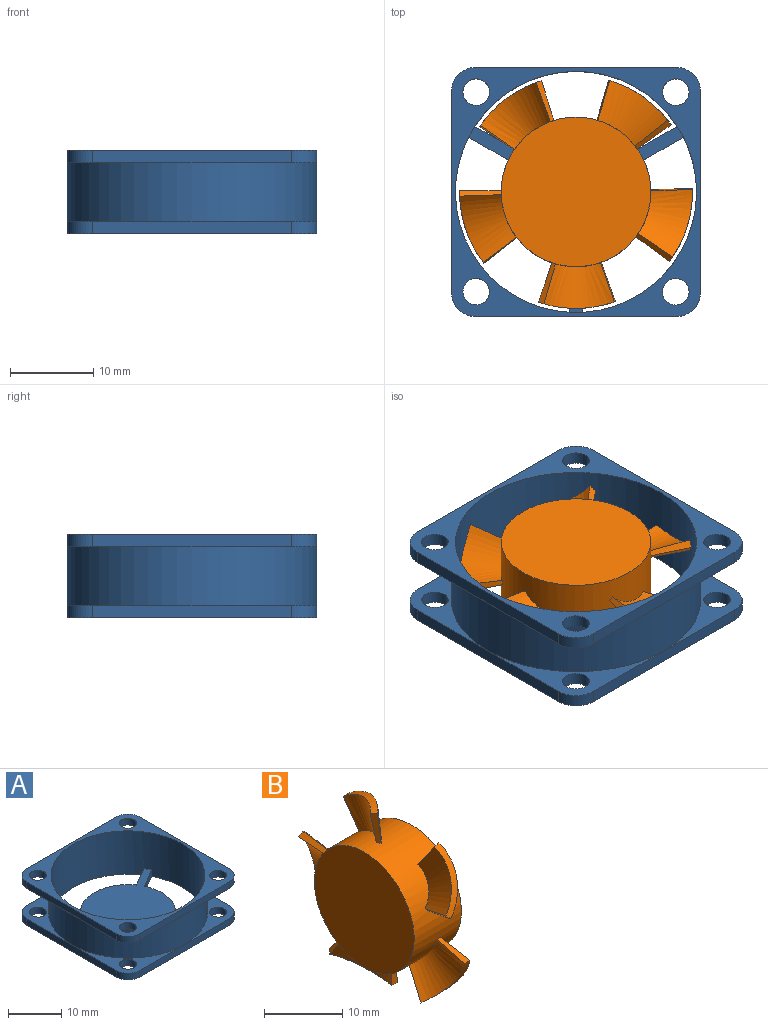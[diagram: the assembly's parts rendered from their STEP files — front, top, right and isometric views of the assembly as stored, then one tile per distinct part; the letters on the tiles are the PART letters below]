
ASSEMBLY  parts=2 mates=1
PART A: 46 faces, bbox 30x30x10 mm
  f0: cylinder r=9mm len=12.8mm, axis (0,0,-1), area 26mm2, adj f11,f37,f39,f41
  f1: cylinder r=1.6mm len=3.2mm, axis (0,0,-1), area 15.1mm2, adj f11,f13
  f2: cylinder r=1.6mm len=3.2mm, axis (0,0,-1), area 15.1mm2, adj f12,f14
  f3: cylinder r=1.6mm len=3.2mm, axis (0,0,-1), area 15.1mm2, adj f11,f15
  f4: cylinder r=1.6mm len=3.2mm, axis (0,0,-1), area 15.1mm2, adj f12,f16
  f5: cylinder r=1.6mm len=3.2mm, axis (0,0,-1), area 15.1mm2, adj f11,f17
  f6: cylinder r=1.6mm len=3.2mm, axis (0,0,-1), area 15.1mm2, adj f12,f18
  f7: cylinder r=1.6mm len=3.2mm, axis (0,0,-1), area 15.1mm2, adj f11,f19
  f8: cylinder r=1.6mm len=3.2mm, axis (0,0,-1), area 15.1mm2, adj f12,f20
  f9: cylinder r=15mm len=30mm, axis (0,0,1), area 659.7mm2, adj f13,f14,f15,f16,f17,f18,f19,f20
  f10: cylinder r=14.5mm len=29mm, axis (0,0,-1), area 904.3mm2, adj f11,f12,f37,f38,f39,f40,f41,f42
  f11: plane 30x30mm, normal (0,0,-1), area 478.8mm2, adj f0,f1,f3,f5,f7,f10,f21,f23
  f12: plane 30x30mm, normal (0,0,1), area 199.6mm2, adj f2,f4,f6,f8,f10,f22,f24,f26
  f13: plane 15x15mm, normal (0,0,1), area 38.3mm2, adj f1,f9,f25,f27,f29
  f14: plane 15x15mm, normal (0,0,-1), area 38.3mm2, adj f2,f9,f26,f28,f30
  f15: plane 15x15mm, normal (0,0,1), area 38.3mm2, adj f3,f9,f21,f23,f25
  f16: plane 15x15mm, normal (0,0,-1), area 38.3mm2, adj f4,f9,f22,f24,f26
  f17: plane 15x15mm, normal (0,0,1), area 38.3mm2, adj f5,f9,f21,f33,f35
  f18: plane 15x15mm, normal (0,0,-1), area 38.3mm2, adj f6,f9,f22,f34,f36
  f19: plane 15x15mm, normal (0,0,1), area 38.3mm2, adj f7,f9,f29,f31,f33
  f20: plane 15x15mm, normal (0,0,-1), area 38.3mm2, adj f8,f9,f30,f32,f34
  f21: plane 24x1.5mm, normal (0,-1,0), area 36mm2, adj f11,f15,f17,f23,f35
  f22: plane 24x1.5mm, normal (0,-1,0), area 36mm2, adj f12,f16,f18,f24,f36
  f23: cylinder r=3mm len=3mm, axis (0,0,-1), area 7.1mm2, adj f11,f15,f21,f25
  f24: cylinder r=3mm len=3mm, axis (0,0,-1), area 7.1mm2, adj f12,f16,f22,f26
  f25: plane 24x1.5mm, normal (-1,0,0), area 36mm2, adj f11,f13,f15,f23,f27
  f26: plane 24x1.5mm, normal (-1,0,0), area 36mm2, adj f12,f14,f16,f24,f28
  f27: cylinder r=3mm len=3mm, axis (0,0,-1), area 7.1mm2, adj f11,f13,f25,f29
  f28: cylinder r=3mm len=3mm, axis (0,0,-1), area 7.1mm2, adj f12,f14,f26,f30
  f29: plane 24x1.5mm, normal (0,1,0), area 36mm2, adj f11,f13,f19,f27,f31
  f30: plane 24x1.5mm, normal (0,1,0), area 36mm2, adj f12,f14,f20,f28,f32
  f31: cylinder r=3mm len=3mm, axis (0,0,-1), area 7.1mm2, adj f11,f19,f29,f33
  f32: cylinder r=3mm len=3mm, axis (0,0,-1), area 7.1mm2, adj f12,f20,f30,f34
  f33: plane 24x1.5mm, normal (1,0,0), area 36mm2, adj f11,f17,f19,f31,f35
  f34: plane 24x1.5mm, normal (1,0,0), area 36mm2, adj f12,f18,f20,f32,f36
  f35: cylinder r=3mm len=3mm, axis (0,0,-1), area 7.1mm2, adj f11,f17,f21,f33
  f36: cylinder r=3mm len=3mm, axis (0,0,-1), area 7.1mm2, adj f12,f18,f22,f34
  f37: plane 5.51x1.5mm, normal (-1,0,0), area 8.3mm2, adj f0,f10,f11,f39
  f38: plane 5.51x1.5mm, normal (1,0,0), area 8.3mm2, adj f10,f11,f39,f44
  f39: plane 25.83x23.5mm, normal (0,0,1), area 279.2mm2, adj f0,f10,f37,f38,f40,f41,f42,f43
  f40: plane 4.77x2.76mm, normal (0.5,0.87,0), area 8.3mm2, adj f10,f11,f39,f45
  f41: plane 4.77x2.76mm, normal (-0.5,-0.87,0), area 8.3mm2, adj f0,f10,f11,f39
  f42: plane 4.77x2.76mm, normal (0.5,-0.87,0), area 8.3mm2, adj f10,f11,f39,f44
  f43: plane 4.77x2.76mm, normal (-0.5,0.87,0), area 8.3mm2, adj f10,f11,f39,f45
  f44: cylinder r=9mm len=12.8mm, axis (0,0,-1), area 26mm2, adj f11,f38,f39,f42
  f45: cylinder r=9mm len=14.78mm, axis (0,0,-1), area 26mm2, adj f11,f39,f40,f43
PART B: 28 faces, bbox 8.5x28.2x28.9 mm
  f0: cylinder r=14mm len=8.81mm, axis (1,0,0), area 9.8mm2, adj f18,f19,f20,f21
  f1: cylinder r=9mm len=18mm, axis (-1,0,0), area 460.6mm2, adj f2,f3,f4,f5,f6,f7,f8,f9
  f2: bspline ~8.51x4.96mm, area 35.5mm2, adj f1,f3,f4,f27
  f3: plane 4.76x1.78mm, normal (-0.16,-0.32,-0.93), area 3.9mm2, adj f1,f2,f5,f27
  f4: plane 4.94x2.04mm, normal (-0.73,-0.32,0.61), area 3.9mm2, adj f1,f2,f5,f27
  f5: bspline ~9.27x4.79mm, area 38.4mm2, adj f1,f3,f4,f27
  f6: bspline ~8.28x6.82mm, area 36.8mm2, adj f1,f7,f8,f26
  f7: plane 4.05x3.14mm, normal (-0.16,0.79,-0.59), area 3.9mm2, adj f1,f6,f9,f26
  f8: plane 5.01x1.38mm, normal (-0.73,-0.68,-0.11), area 3.9mm2, adj f1,f6,f9,f26
  f9: bspline ~8.82x6.88mm, area 40.1mm2, adj f1,f7,f8,f26
  f10: bspline ~8.66x8mm, area 36.8mm2, adj f1,f11,f12,f25
  f11: plane 4.19x2.94mm, normal (-0.16,0.81,0.57), area 3.9mm2, adj f1,f10,f13,f25
  f12: plane 4.92x2.14mm, normal (-0.73,-0.1,-0.68), area 3.9mm2, adj f1,f10,f13,f25
  f13: bspline ~9x8.31mm, area 40.1mm2, adj f1,f11,f12,f25
  f14: bspline ~9.1x9.03mm, area 36.8mm2, adj f1,f15,f16,f24
  f15: plane 4.83x1.55mm, normal (-0.16,-0.29,0.94), area 3.9mm2, adj f1,f14,f17,f24
  f16: plane 4.35x3.44mm, normal (-0.73,0.62,-0.31), area 3.9mm2, adj f1,f14,f17,f24
  f17: bspline ~8.92x8.36mm, area 40.1mm2, adj f1,f15,f16,f24
  f18: bspline ~8.45x8.05mm, area 39.2mm2, adj f0,f1,f19,f20
  f19: plane 5x1.07mm, normal (-0.16,-0.99,0.01), area 3.9mm2, adj f0,f1,f18,f21
  f20: plane 4.41x3.36mm, normal (-0.73,0.48,0.49), area 3.9mm2, adj f0,f1,f18,f21
  f21: bspline ~9.31x7.7mm, area 43.3mm2, adj f0,f1,f19,f20
  f22: plane 18x18mm, normal (1,0,0), area 254.5mm2, adj f1
  f23: plane 18x18mm, normal (-1,0,0), area 254.5mm2, adj f1
  f24: cylinder r=14mm len=7.52mm, axis (1,0,0), area 10mm2, adj f14,f15,f16,f17
  f25: cylinder r=14mm len=7.43mm, axis (1,0,0), area 10mm2, adj f10,f11,f12,f13
  f26: cylinder r=14mm len=8.76mm, axis (1,0,0), area 10mm2, adj f6,f7,f8,f9
  f27: cylinder r=14mm len=9.24mm, axis (1,0,0), area 10mm2, adj f2,f3,f4,f5
PLACE A t=(4.87,1.14,-11.04)mm
PLACE B rot(axis=(-0.71,0,0.71),180deg) t=(4.87,1.14,-11.04)mm
MATE revolute B.f1 <-> A.f0  axis (0,0,-1) through (4.87,1.14,-9.54)mm
